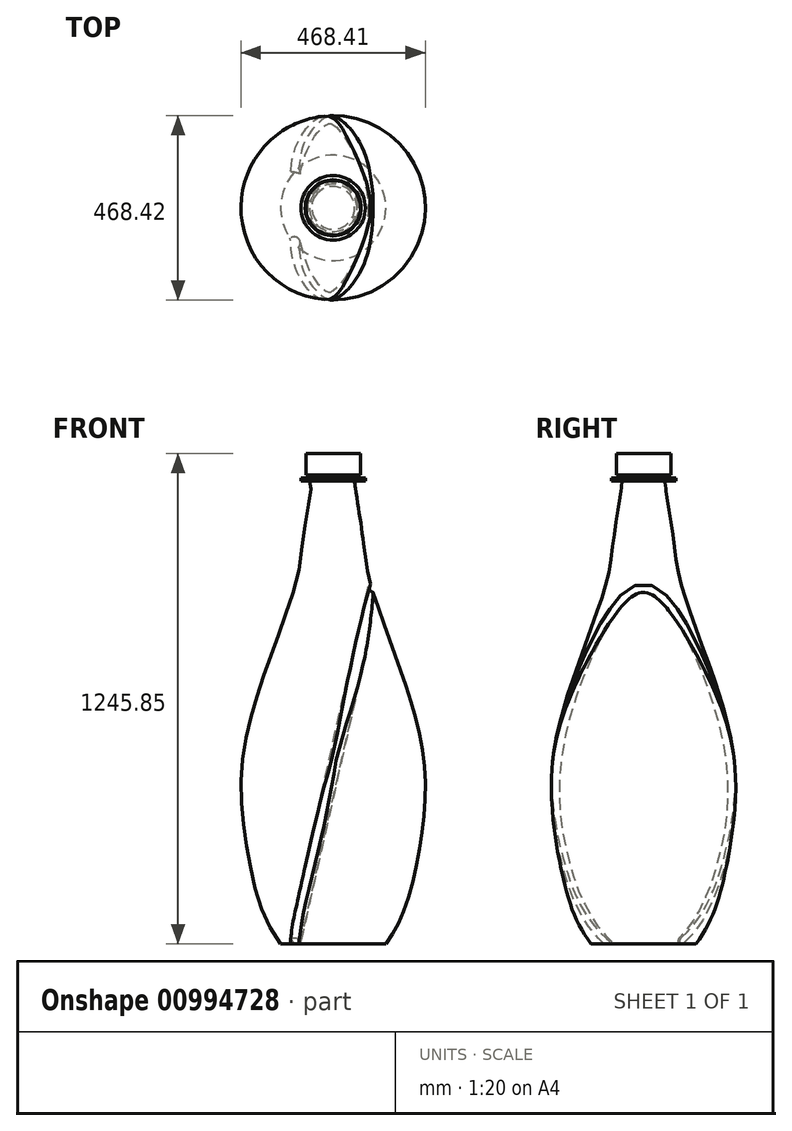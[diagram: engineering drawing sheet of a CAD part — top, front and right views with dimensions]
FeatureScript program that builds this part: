
annotation { "Feature Type Name" : "Feature", "Feature Type Description" : "" }
export const myFeature = defineFeature(function(context is Context, id is Id, definition is map)
    precondition{}
    {
        {
            var Q0;
            Q0=qCreatedBy(makeId("Front.planeOp"),FACE);
            var sketch = newSketch(context, id + "F0", { "sketchPlane" : qUnion([Q0])});
            skLineSegment(sketch, "E0", {"start": v(-4.47, 14.62) * mm, "end": v(129.22, 14.62) * mm});
            skLineSegment(sketch, "E1", {"start": v(55.77, 1190.17) * mm, "end": v(77.37, 1190.17) * mm});
            skLineSegment(sketch, "E2", {"start": v(-4.47, 14.62) * mm, "end": v(-4.47, 1260.47) * mm});
            skFitSpline(sketch, "E3", {"points": [v(129.22, 14.62) * mm, v(205.5, 241.58) * mm, v(219.7, 436.7) * mm, v(178.06, 659.76) * mm, v(95.94, 927.14) * mm, v(72.01, 1040.92) * mm, v(53.53, 1162.5) * mm, v(50.88, 1183.43) * mm, v(55.77, 1190.17) * mm], "startDerivative": vector(716.75, 1242.6) * mm, "endDerivative": vector(459.17, 147.66) * mm});
            skLineSegment(sketch, "E4", {"start": v(77.37, 1190.17) * mm, "end": v(77.37, 1197.74) * mm});
            skLineSegment(sketch, "E5", {"start": v(77.37, 1197.74) * mm, "end": v(66.68, 1197.74) * mm});
            skLineSegment(sketch, "E6", {"start": v(66.68, 1197.74) * mm, "end": v(60.6, 1201.32) * mm});
            skLineSegment(sketch, "E7", {"start": v(60.6, 1201.32) * mm, "end": v(60.6, 1205.98) * mm});
            skLineSegment(sketch, "E8", {"start": v(60.6, 1205.98) * mm, "end": v(65.73, 1205.98) * mm});
            skLineSegment(sketch, "E9", {"start": v(64.87, 1205.98) * mm, "end": v(64.87, 1260.28) * mm});
            skLineSegment(sketch, "E10", {"start": v(64.87, 1260.28) * mm, "end": v(-4.47, 1260.47) * mm});
            skSolve(sketch);
        }
        {
            var Q0;
            Q0=qCreatedBy(makeId("Front.planeOp"),FACE);
            var sketch = newSketch(context, id + "F1", { "sketchPlane" : qUnion([Q0])});
            skLineSegment(sketch, "E11.0", {"start": v(-4.47, 14.62) * mm, "end": v(-4.47, 1260.47) * mm});
            skFitSpline(sketch, "E12.0", {"points": [v(129.22, 14.62) * mm, v(170.03, 85.36) * mm, v(211.68, 239.85) * mm, v(229.23, 440.1) * mm, v(185.4, 655.74) * mm, v(91.4, 926.9) * mm, v(73.22, 1029.97) * mm, v(54.03, 1159.21) * mm, v(50.54, 1182.54) * mm, v(50.9, 1188.6) * mm, v(55.77, 1190.17) * mm]});
            skLineSegment(sketch, "E13.0", {"start": v(64.87, 1260.28) * mm, "end": v(-4.47, 1260.47) * mm});
            skLineSegment(sketch, "E14.0", {"start": v(64.87, 1205.98) * mm, "end": v(64.87, 1260.28) * mm});
            skLineSegment(sketch, "E15.0", {"start": v(60.6, 1201.32) * mm, "end": v(60.6, 1205.98) * mm});
            skLineSegment(sketch, "E16.0", {"start": v(60.6, 1205.98) * mm, "end": v(64.87, 1205.98) * mm});
            skLineSegment(sketch, "E17.0", {"start": v(66.68, 1197.74) * mm, "end": v(60.6, 1201.32) * mm});
            skLineSegment(sketch, "E18.0", {"start": v(77.37, 1197.74) * mm, "end": v(66.68, 1197.74) * mm});
            skLineSegment(sketch, "E19.0", {"start": v(55.77, 1190.17) * mm, "end": v(77.37, 1190.17) * mm});
            skLineSegment(sketch, "E20", {"start": v(77.37, 1197.74) * mm, "end": v(77.37, 1190.17) * mm});
            skLineSegment(sketch, "E21", {"start": v(129.22, 14.62) * mm, "end": v(-4.47, 14.62) * mm});
            skSolve(sketch);
        }
        {
            var Q0;
            Q0=makeQuery(id+"F1.imprint","IMPRINT",FACE,{"disambiguationData":[TD([[makeQuery(id+"F1.imprint","IMPRINT",EDGE,{"derivedFrom":sQuery(id+"F1.wireOp",EDGE,"E11.0")}),-1.0]])]});
            var Q1;
            Q1=sQuery(id+"F1.wireOp",EDGE,"E11.0");
            revolve(context, id + "F2", {"surfaceOperationType" : NewSurfaceOperationType.NEW, "entities" : qUnion([Q0]), "axis" : qUnion([Q1]), "revolveType" : RevolveType.FULL});
        }
        {
            var Q0;
            Q0=qCreatedBy(makeId("Front.planeOp"),FACE);
            cPlane(context, id + "F3", {"entities" : qUnion([Q0]), "cplaneType" : CPlaneType.OFFSET, "offset" : 250 * mm, "width" : 150 * mm, "height" : 150 * mm});
        }
        {
            var Q0;
            Q0=qCreatedBy(id+"F3.planeOp",FACE);
            var sketch = newSketch(context, id + "F4", { "sketchPlane" : qUnion([Q0])});
            skFitSpline(sketch, "E22", {"points": [v(-103.83, 14.62) * mm, v(-106.95, 260.33) * mm, v(-4.48, 580.79) * mm, v(91.25, 882.5) * mm], "startDerivative": vector(-87.8, 926.59) * mm, "endDerivative": vector(183.77, 1286.36) * mm, "construction": true});
            skLineSegment(sketch, "E23", {"start": v(91.25, 882.5) * mm, "end": v(194.24, 882.5) * mm, "construction": true});
            skLineSegment(sketch, "E24", {"start": v(91.25, 882.5) * mm, "end": v(-103.83, 14.62) * mm});
            skSolve(sketch);
        }
        {
            var Q0;
            Q0=sQuery(id+"F4.wireOp",EDGE,"E24");
            var Q1;
            Q1=makeQuery(id+"F2.opRevolve","SWEPT_BODY",BODY,{"disambiguationData":[OSD([sQuery(id+"F1.wireOp",EDGE,"E11.0"),sQuery(id+"F1.wireOp",EDGE,"E12.0"),sQuery(id+"F1.wireOp",EDGE,"E13.0"),sQuery(id+"F1.wireOp",EDGE,"E14.0"),sQuery(id+"F1.wireOp",EDGE,"E15.0"),sQuery(id+"F1.wireOp",EDGE,"E16.0"),sQuery(id+"F1.wireOp",EDGE,"E17.0"),sQuery(id+"F1.wireOp",EDGE,"E18.0"),sQuery(id+"F1.wireOp",EDGE,"E19.0"),sQuery(id+"F1.wireOp",EDGE,"E20"),sQuery(id+"F1.wireOp",EDGE,"E21")])]});
            extrude(context, id + "F5", {"bodyType" : ToolBodyType.SURFACE, "surfaceEntities" : qUnion([Q0]), "endBound" : BoundingType.UP_TO_BODY, "oppositeDirection" : true, "depth" : 25 * mm, "endBoundEntityBody" : qUnion([Q1]), "offsetDistance" : 25 * mm});
        }
        {
            var Q0;
            Q0=makeQuery(id+"F5.opExtrude","CAP_EDGE",EDGE,{"disambiguationData":[OSD([sQuery(id+"F4.wireOp",EDGE,"E24")])],"isStart":true});
            cPoint(context, id + "F6", {"entities" : qUnion([Q0]), "parameter" : 0.5});
        }
        {
            var Q0;
            Q0=makeQuery(id+"F5.opExtrude","SWEPT_FACE",FACE,{"disambiguationData":[OSD([sQuery(id+"F4.wireOp",EDGE,"E24")])]});
            var Q1;
            Q1 = qCreatedBy(id + "F6" ,VERTEX);
            cPlane(context, id + "F7", {"entities" : qUnion([Q0, Q1]), "cplaneType" : CPlaneType.PLANE_POINT, "offset" : 25 * mm, "width" : 150 * mm, "height" : 150 * mm});
        }
        {
            var Q0;
            Q0=qCreatedBy(makeId("Right.planeOp"),FACE);
            var sketch = newSketch(context, id + "F8", { "sketchPlane" : qUnion([Q0])});
            skFitSpline(sketch, "E25", {"points": [v(133.7, 14.62) * mm, v(117.1, -13.16) * mm], "startDerivative": vector(-16.6, -27.79) * mm, "endDerivative": vector(-16.6, -27.79) * mm});
            skLineSegment(sketch, "E26", {"start": v(0, 0) * mm, "end": v(0, 32.04) * mm, "construction": true});
            skSolve(sketch);
        }
        {
            var Q0;
            Q0=qCreatedBy(id+"F7.planeOp",FACE);
            var sketch = newSketch(context, id + "F9", { "sketchPlane" : qUnion([Q0])});
            skFitSpline(sketch, "E27", {"points": [v(89.46, -8.5) * mm, v(93.48, -4.8) * mm, v(101.19, 2.87) * mm, v(111.9, 15.02) * mm, v(121.85, 27.73) * mm, v(129.6, 38.75) * mm, v(135.5, 47.8) * mm, v(139.76, 54.68) * mm, v(143.21, 60.51) * mm, v(145.9, 65.23) * mm, v(148.55, 69.98) * mm, v(151.76, 75.96) * mm, v(155.47, 83.18) * mm, v(159.05, 90.45) * mm, v(163.63, 100.2) * mm, v(169.06, 112.51) * mm, v(175.1, 127.45) * mm, v(180.72, 142.54) * mm, v(187.68, 162.84) * mm, v(193.9, 183.41) * mm, v(199.5, 204.2) * mm, v(202.74, 217.3) * mm, v(205.2, 227.8) * mm, v(206.97, 235.73) * mm, v(208.67, 243.65) * mm, v(210.84, 254.22) * mm, v(213.36, 267.45) * mm, v(216.96, 288.66) * mm, v(220.63, 315.23) * mm, v(223.1, 341.9) * mm, v(224.33, 363.3) * mm, v(224.86, 379.4) * mm, v(224.98, 395.51) * mm, v(224.7, 411.66) * mm, v(224.12, 425.15) * mm, v(223.53, 434.6) * mm, v(223.14, 440.02) * mm, v(222.5, 448.11) * mm, v(221.37, 460.2) * mm, v(219.47, 476.24) * mm, v(217.22, 492.18) * mm, v(213.76, 513.32) * mm, v(208.63, 539.54) * mm, v(201.32, 570.7) * mm, v(192.97, 601.6) * mm, v(183.66, 632.27) * mm, v(175.15, 657.62) * mm, v(167.9, 677.8) * mm, v(162.27, 692.88) * mm, v(157.4, 705.4) * mm, v(153.38, 715.39) * mm, v(149.3, 725.36) * mm, v(144.07, 737.76) * mm, v(135.4, 757.46) * mm, v(126.3, 776.92) * mm, v(116.64, 796.09) * mm, v(109.08, 810.3) * mm, v(101.18, 824.35) * mm, v(94.24, 835.86) * mm, v(88.44, 844.94) * mm, v(84.7, 850.56) * mm, v(81.63, 855.01) * mm, v(78.5, 859.44) * mm, v(74.5, 864.88) * mm, v(69.54, 871.27) * mm, v(64.37, 877.5) * mm, v(59, 883.53) * mm, v(54.3, 888.37) * mm, v(50.39, 892.1) * mm, v(47.37, 894.84) * mm, v(44.26, 897.49) * mm, v(40.03, 900.86) * mm, v(35.62, 904) * mm, v(31.02, 906.86) * mm, v(28.06, 908.51) * mm, v(25.62, 909.74) * mm, v(23.16, 910.9) * mm, v(20.05, 912.2) * mm, v(16.23, 913.54) * mm, v(12.97, 914.43) * mm, v(10.32, 915.01) * mm, v(8.32, 915.37) * mm, v(6.28, 915.66) * mm, v(4.26, 915.86) * mm, v(2.23, 916) * mm, v(-0.46, 916.05) * mm, v(-3.81, 915.94) * mm, v(-7.82, 915.49) * mm, v(-11.15, 914.86) * mm, v(-13.8, 914.2) * mm, v(-16.42, 913.46) * mm, v(-19.62, 912.37) * mm, v(-23.36, 910.83) * mm, v(-27, 909.08) * mm, v(-29.97, 907.45) * mm, v(-32.3, 906.07) * mm, v(-34.6, 904.62) * mm, v(-37.42, 902.72) * mm, v(-41.77, 899.53) * mm, v(-46.97, 895.27) * mm, v(-52.89, 889.8) * mm, v(-57.6, 884.98) * mm, v(-61.24, 881) * mm, v(-64.83, 876.94) * mm, v(-69.14, 871.76) * mm, v(-74.1, 865.41) * mm, v(-80.46, 856.8) * mm, v(-87.99, 845.78) * mm, v(-96.5, 832.24) * mm, v(-104.57, 818.43) * mm, v(-112.27, 804.4) * mm, v(-119.66, 790.18) * mm, v(-125.58, 778.18) * mm, v(-130.19, 768.51) * mm, v(-134.72, 758.8) * mm, v(-140.22, 746.6) * mm, v(-146.57, 731.9) * mm, v(-154.75, 712.2) * mm, v(-164.45, 687.42) * mm, v(-175.27, 657.44) * mm, v(-185.25, 627.22) * mm, v(-194.35, 596.73) * mm, v(-202.5, 565.96) * mm, v(-208.44, 540.06) * mm, v(-212.6, 519.17) * mm, v(-215.42, 503.41) * mm, v(-217.91, 487.55) * mm, v(-219.7, 474.26) * mm, v(-220.96, 463.56) * mm, v(-221.8, 455.54) * mm, v(-222.54, 447.53) * mm, v(-223.4, 436.85) * mm, v(-224.23, 423.53) * mm, v(-224.8, 407.56) * mm, v(-224.99, 391.62) * mm, v(-224.7, 370.4) * mm, v(-223.36, 343.95) * mm, v(-220.27, 312.3) * mm, v(-216.54, 286) * mm, v(-212.9, 265) * mm, v(-209.87, 249.27) * mm, v(-206.53, 233.57) * mm, v(-202.9, 217.87) * mm, v(-199, 202.28) * mm, v(-193.4, 181.63) * mm, v(-185.59, 156.1) * mm, v(-176.56, 130.98) * mm, v(-169.5, 113.65) * mm, v(-165.23, 103.83) * mm, v(-161.9, 96.5) * mm, v(-159.03, 90.44) * mm, v(-156.66, 85.6) * mm, v(-154.25, 80.8) * mm, v(-151.17, 74.83) * mm, v(-146.06, 65.4) * mm, v(-139.36, 53.85) * mm, v(-130.77, 40.39) * mm, v(-121.57, 27.35) * mm, v(-111.7, 14.8) * mm, v(-101.1, 2.78) * mm, v(-93.45, -4.82) * mm, v(-89.46, -8.5) * mm]});
            skSolve(sketch);
        }
        {
            var Q0;
            Q0=makeQuery(id+"F2.opRevolve","SWEPT_FACE",FACE,{"disambiguationData":[OSD([sQuery(id+"F1.wireOp",EDGE,"E21")])]});
            var sketch = newSketch(context, id + "F10", { "sketchPlane" : qUnion([Q0])});
            skCircle(sketch, "E28", {"center": v(-103.83, 89.46) * mm, "radius": 15.85 * mm});
            skSolve(sketch);
        }
        {
            var Q0;
            Q0 = qSketchRegion(id + "F10", true);
            var Q1;
            Q1=sQuery(id+"F9.wireOp",EDGE,"E27");
            sweep(context, id + "F11", {"operationType" : NewBodyOperationType.REMOVE, "profiles" : qUnion([Q0]), "path" : qUnion([Q1])});
        }
    });
